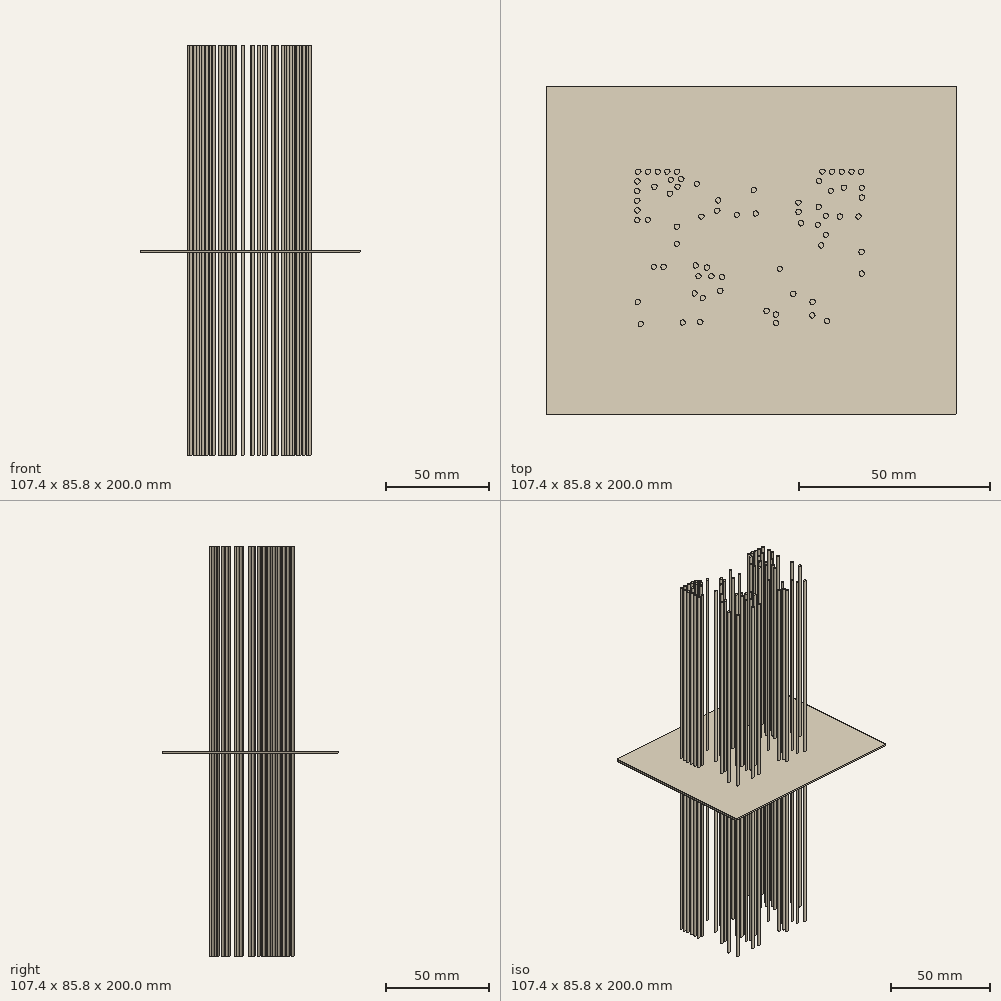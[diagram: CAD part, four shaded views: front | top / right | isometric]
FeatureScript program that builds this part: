
annotation { "Feature Type Name" : "Feature", "Feature Type Description" : "" }
export const myFeature = defineFeature(function(context is Context, id is Id, definition is map)
    precondition{}
    {
        {
            var Q0;
            Q0=qCreatedBy(makeId("Top.planeOp"),FACE);
            var sketch = newSketch(context, id + "F0", { "sketchPlane" : qUnion([Q0])});
            skLineSegment(sketch, "E0.bottom", {"start": v(-54.09, 41.2) * mm, "end": v(53.34, 41.2) * mm});
            skLineSegment(sketch, "E0.top", {"start": v(-54.09, -44.56) * mm, "end": v(53.34, -44.56) * mm});
            skLineSegment(sketch, "E0.left", {"start": v(-54.09, 41.2) * mm, "end": v(-54.09, -44.56) * mm});
            skLineSegment(sketch, "E0.right", {"start": v(53.34, 41.2) * mm, "end": v(53.34, -44.56) * mm});
            skLineSegment(sketch, "E1", {"start": v(0, 69) * mm, "end": v(0, -69.54) * mm, "construction": true});
            skSolve(sketch);
        }
        {
            var Q0;
            Q0 = qSketchRegion(id + "F0", true);
            extrude(context, id + "F1", {"entities" : qUnion([Q0]), "depth" : 1 * mm});
        }
        {
            var Q0;
            Q0=qCreatedBy(makeId("Top.planeOp"),FACE);
            var sketch = newSketch(context, id + "F2", { "sketchPlane" : qUnion([Q0])});
            skCircle(sketch, "E2", {"center": v(-18.67, -0.39) * mm, "radius": 0.7 * mm});
            skCircle(sketch, "E3", {"center": v(-17.98, 9.7) * mm, "radius": 0.7 * mm});
            skCircle(sketch, "E4", {"center": v(-19.89, 2.35) * mm, "radius": 0.7 * mm});
            skCircle(sketch, "E5", {"center": v(-23.55, 7.2) * mm, "radius": 0.7 * mm});
            skCircle(sketch, "E6", {"center": v(-19.88, 7.33) * mm, "radius": 0.7 * mm});
            skCircle(sketch, "E7", {"center": v(-18.98, 18.95) * mm, "radius": 0.7 * mm});
            skCircle(sketch, "E8", {"center": v(-26.6, 18.95) * mm, "radius": 0.7 * mm});
            skCircle(sketch, "E9", {"center": v(-21.52, 18.95) * mm, "radius": 0.7 * mm});
            skCircle(sketch, "E10", {"center": v(-29.14, 18.95) * mm, "radius": 0.7 * mm});
            skCircle(sketch, "E11", {"center": v(-24.07, 18.95) * mm, "radius": 0.7 * mm});
            skCircle(sketch, "E12", {"center": v(-18.1, 16.48) * mm, "radius": 0.7 * mm});
            skCircle(sketch, "E13", {"center": v(-4.33, -17.52) * mm, "radius": 0.7 * mm});
            skCircle(sketch, "E14", {"center": v(-6.83, -18.48) * mm, "radius": 0.7 * mm});
            skCircle(sketch, "E15", {"center": v(-24.6, 14.78) * mm, "radius": 0.7 * mm});
            skCircle(sketch, "E16", {"center": v(29.52, 16.41) * mm, "radius": 0.7 * mm});
            skCircle(sketch, "E17", {"center": v(29.52, 13.87) * mm, "radius": 0.7 * mm});
            skCircle(sketch, "E18", {"center": v(-21.2, 13.95) * mm, "radius": 0.7 * mm});
            skCircle(sketch, "E19", {"center": v(29.52, 6.25) * mm, "radius": 0.7 * mm});
            skCircle(sketch, "E20", {"center": v(-29.23, -2.08) * mm, "radius": 0.7 * mm});
            skCircle(sketch, "E21", {"center": v(-16.32, -18.73) * mm, "radius": 0.7 * mm});
            skCircle(sketch, "E22", {"center": v(3.45, 7.62) * mm, "radius": 0.7 * mm});
            skCircle(sketch, "E23", {"center": v(-6.83, -20.75) * mm, "radius": 0.7 * mm});
            skCircle(sketch, "E24", {"center": v(-29.27, -7.75) * mm, "radius": 0.7 * mm});
            skCircle(sketch, "E25", {"center": v(-11.35, -13.05) * mm, "radius": 0.7 * mm});
            skCircle(sketch, "E26", {"center": v(18, 17) * mm, "radius": 0.7 * mm});
            skCircle(sketch, "E27", {"center": v(25.05, 15) * mm, "radius": 0.7 * mm});
            skCircle(sketch, "E28", {"center": v(20.73, 16.75) * mm, "radius": 0.7 * mm});
            skCircle(sketch, "E29", {"center": v(19, 15) * mm, "radius": 0.7 * mm});
            skCircle(sketch, "E30", {"center": v(13.47, -8.45) * mm, "radius": 0.7 * mm});
            skCircle(sketch, "E31", {"center": v(10.1, -8.45) * mm, "radius": 0.7 * mm});
            skCircle(sketch, "E32", {"center": v(11.3, -6.17) * mm, "radius": 0.7 * mm});
            skCircle(sketch, "E33", {"center": v(7.78, -12.28) * mm, "radius": 0.7 * mm});
            skCircle(sketch, "E34", {"center": v(8.32, 11.43) * mm, "radius": 0.7 * mm});
            skCircle(sketch, "E35", {"center": v(8.57, 8.72) * mm, "radius": 0.7 * mm});
            skCircle(sketch, "E36", {"center": v(13.9, 15.7) * mm, "radius": 0.7 * mm});
            skCircle(sketch, "E37", {"center": v(12.72, 7.17) * mm, "radius": 0.7 * mm});
            skCircle(sketch, "E38", {"center": v(14.22, -5.62) * mm, "radius": 0.7 * mm});
            skCircle(sketch, "E39", {"center": v(21.66, 18.95) * mm, "radius": 0.7 * mm});
            skCircle(sketch, "E40", {"center": v(26.73, 18.95) * mm, "radius": 0.7 * mm});
            skCircle(sketch, "E41", {"center": v(19.11, 18.95) * mm, "radius": 0.7 * mm});
            skCircle(sketch, "E42", {"center": v(24.2, 18.95) * mm, "radius": 0.7 * mm});
            skCircle(sketch, "E43", {"center": v(29.27, 18.95) * mm, "radius": 0.7 * mm});
            skCircle(sketch, "E44", {"center": v(20.98, 13.2) * mm, "radius": 0.7 * mm});
            skCircle(sketch, "E45", {"center": v(-29.34, 12.18) * mm, "radius": 0.7 * mm});
            skCircle(sketch, "E46", {"center": v(29.52, 11.33) * mm, "radius": 0.7 * mm});
            skCircle(sketch, "E47", {"center": v(-29.34, 14.72) * mm, "radius": 0.7 * mm});
            skCircle(sketch, "E48", {"center": v(29.52, 8.79) * mm, "radius": 0.7 * mm});
            skCircle(sketch, "E49", {"center": v(-1.5, 8) * mm, "radius": 0.7 * mm});
            skCircle(sketch, "E50", {"center": v(-1, 14.1) * mm, "radius": 0.7 * mm});
            skCircle(sketch, "E51", {"center": v(-7.83, -6.5) * mm, "radius": 0.7 * mm});
            skCircle(sketch, "E52", {"center": v(-28.44, 7.2) * mm, "radius": 0.7 * mm});
            skCircle(sketch, "E53", {"center": v(26.75, 6.35) * mm, "radius": 0.7 * mm});
            skCircle(sketch, "E54", {"center": v(19.15, 4.55) * mm, "radius": 0.7 * mm});
            skCircle(sketch, "E55", {"center": v(12.38, -14.2) * mm, "radius": 0.7 * mm});
            skCircle(sketch, "E56", {"center": v(29.43, -15.2) * mm, "radius": 0.7 * mm});
            skCircle(sketch, "E57", {"center": v(28.62, -20.98) * mm, "radius": 0.7 * mm});
            skCircle(sketch, "E58", {"center": v(17.62, -20.57) * mm, "radius": 0.7 * mm});
            skCircle(sketch, "E59", {"center": v(13.03, -20.47) * mm, "radius": 0.7 * mm});
            skCircle(sketch, "E60", {"center": v(-13.38, 5.42) * mm, "radius": 0.7 * mm});
            skCircle(sketch, "E61", {"center": v(-20.2, -20.18) * mm, "radius": 0.7 * mm});
            skCircle(sketch, "E62", {"center": v(25.2, -5.97) * mm, "radius": 0.7 * mm});
            skCircle(sketch, "E63", {"center": v(22.66, -5.97) * mm, "radius": 0.7 * mm});
            skCircle(sketch, "E64", {"center": v(19.15, 0.03) * mm, "radius": 0.7 * mm});
            skCircle(sketch, "E65", {"center": v(14.5, -12.95) * mm, "radius": 0.7 * mm});
            skCircle(sketch, "E66", {"center": v(7.33, -8.68) * mm, "radius": 0.7 * mm});
            skCircle(sketch, "E67", {"center": v(-12.7, 10.85) * mm, "radius": 0.7 * mm});
            skCircle(sketch, "E68", {"center": v(-12.7, 8.4) * mm, "radius": 0.7 * mm});
            skCircle(sketch, "E69", {"center": v(-17.82, 4.97) * mm, "radius": 0.7 * mm});
            skCircle(sketch, "E70", {"center": v(-16.4, -15.18) * mm, "radius": 0.7 * mm});
            skSolve(sketch);
        }
        {
            var Q0;
            Q0 = qSketchRegion(id + "F2", true);
            extrude(context, id + "F3", {"entities" : qUnion([Q0]), "operationType" : NewBodyOperationType.ADD, "depth" : 100 * mm, "hasSecondDirection" : true, "secondDirectionOppositeDirection" : true, "secondDirectionDepth" : 100 * mm});
        }
        {
            var Q0;
            Q0=qCreatedBy(makeId("Top.planeOp"),FACE);
            var sketch = newSketch(context, id + "F4", { "sketchPlane" : qUnion([Q0])});
            skLineSegment(sketch, "E71", {"start": v(0, 69.18) * mm, "end": v(0, -75.48) * mm, "construction": true});
            skSolve(sketch);
        }
        {
            var Q0;
            Q0=makeQuery(id+"F1.opExtrude","SWEPT_BODY",BODY,{"disambiguationData":[OSD([sQuery(id+"F0.wireOp",EDGE,"E0.bottom"),sQuery(id+"F0.wireOp",EDGE,"E0.top"),sQuery(id+"F0.wireOp",EDGE,"E0.left"),sQuery(id+"F0.wireOp",EDGE,"E0.right")])]});
            var Q1;
            Q1=sQuery(id+"F4.wireOp",EDGE,"E71");
            transform(context, id + "F5", {"entities" : qUnion([Q0]), "transformType" : TransformType.ROTATION, "transformAxis" : qUnion([Q1]), "angle" : 180 * degree, "makeCopy" : false});
        }
    });
